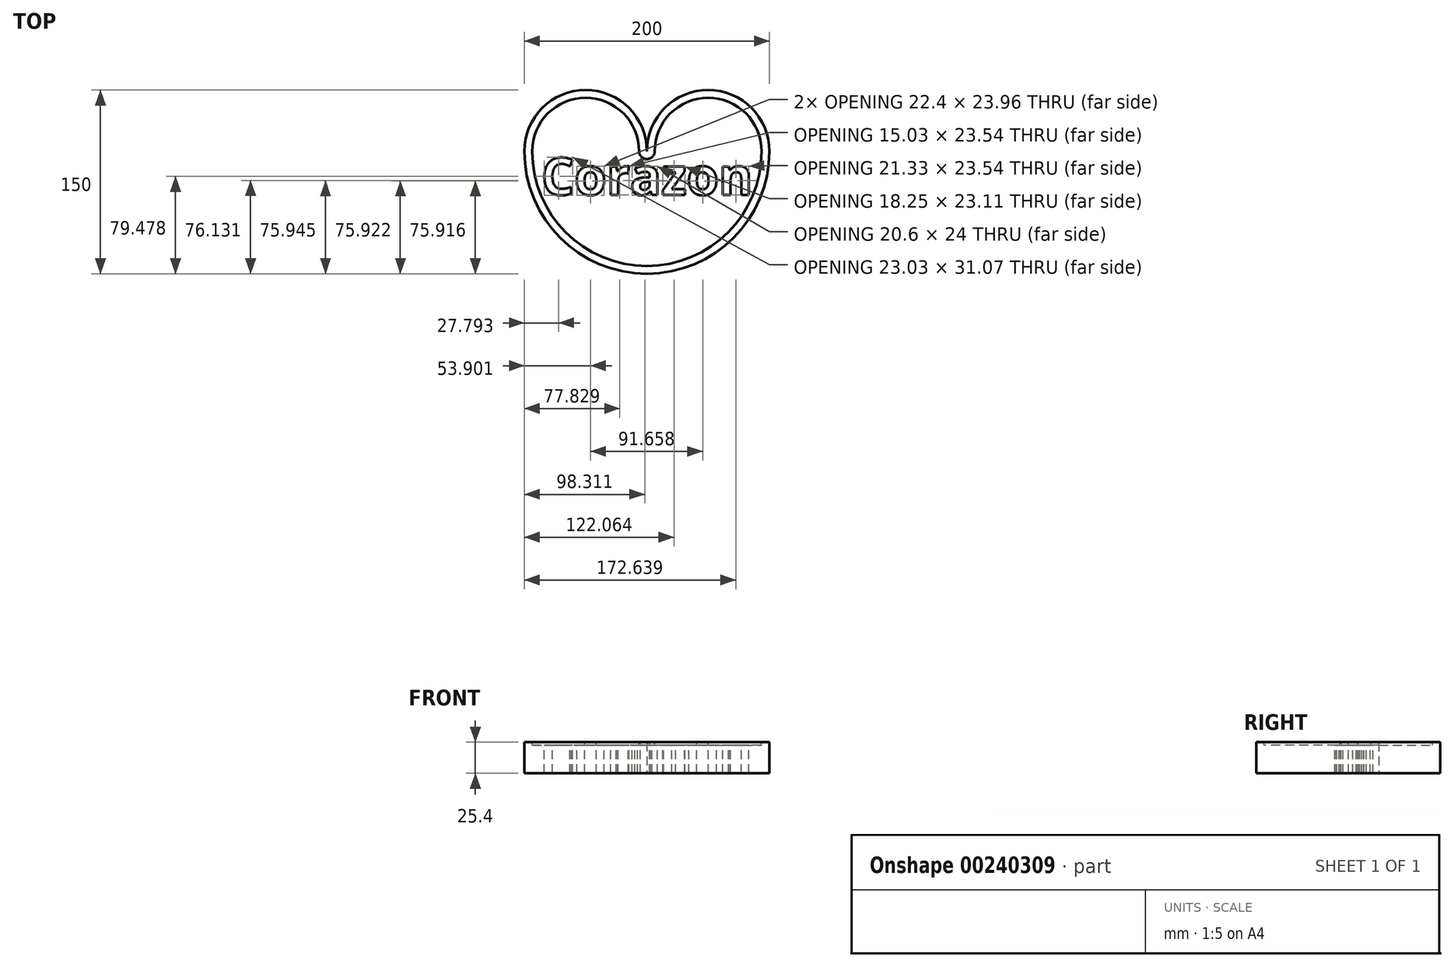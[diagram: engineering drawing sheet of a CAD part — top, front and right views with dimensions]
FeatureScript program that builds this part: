
annotation { "Feature Type Name" : "Feature", "Feature Type Description" : "" }
export const myFeature = defineFeature(function(context is Context, id is Id, definition is map)
    precondition{}
    {
        {
            var Q0;
            Q0=qCreatedBy(makeId("Top.planeOp"),FACE);
            var sketch = newSketch(context, id + "F0", { "sketchPlane" : qUnion([Q0])});
            skLineSegment(sketch, "E0.bottom", {"start": v(50, 50) * mm, "end": v(-50, 50) * mm, "construction": true});
            skLineSegment(sketch, "E0.top", {"start": v(50, -50) * mm, "end": v(-50, -50) * mm, "construction": true});
            skLineSegment(sketch, "E0.left", {"start": v(50, 50) * mm, "end": v(50, -50) * mm, "construction": true});
            skLineSegment(sketch, "E0.right", {"start": v(-50, 50) * mm, "end": v(-50, -50) * mm, "construction": true});
            skPoint(sketch, "E0.middle", {"position": v(0, 0) * mm});
            skArc(sketch, "E1", {"start": v(0, 50) * mm, "mid": v(-50, 100) * mm, "end": v(-100, 50) * mm});
            skArc(sketch, "E2", {"start": v(100, 50) * mm, "mid": v(50, 100) * mm, "end": v(0, 50) * mm});
            skLineSegment(sketch, "E3", {"start": v(-50, 50) * mm, "end": v(50, 50) * mm, "construction": true});
            skPoint(sketch, "E4.start.orphan", {"position": v(50, 0) * mm});
            skPoint(sketch, "E5.start.orphan", {"position": v(-50, 0) * mm});
            skArc(sketch, "E6", {"start": v(-100, 50) * mm, "mid": v(0, -50) * mm, "end": v(100, 50) * mm});
            skSolve(sketch);
        }
        {
            var Q0;
            Q0 = qSketchRegion(id + "F0", true);
            extrude(context, id + "F1", {"entities" : qUnion([Q0]), "depth" : 25.4 * mm});
        }
        {
            var Q0;
            Q0=makeQuery(id+"F1.opExtrude","CAP_FACE",FACE,{"disambiguationData":[OSD([sQuery(id+"F0.wireOp",EDGE,"E1"),sQuery(id+"F0.wireOp",EDGE,"E2"),sQuery(id+"F0.wireOp",EDGE,"E6")])],"isStart":false});
            var sketch = newSketch(context, id + "F2", { "sketchPlane" : qUnion([Q0])});
            skText(sketch, "E7", { "text": "Corazon", "fontName": "OpenSans-Bold.ttf"});
            const initialGuessF2  = {"E7": [-0.08618, 0.01436, 1, 0, 0.03048]};
            skSetInitialGuess(sketch, initialGuessF2);
            skSolve(sketch);
        }
        {
            var Q0;
            Q0 = qSketchRegion(id + "F2", true);
            extrude(context, id + "F3", {"entities" : qUnion([Q0]), "operationType" : NewBodyOperationType.REMOVE, "oppositeDirection" : true, "depth" : 25.4 * mm});
        }
        {
            var Q0;
            {var subQ0=sQuery(id+"F0.wireOp",EDGE,"E1");var subQ1=sQuery(id+"F0.wireOp",EDGE,"E2");var subQ2=sQuery(id+"F0.wireOp",EDGE,"E6");Q0=makeQuery(id+"F3.boolean.opBoolean","SPLIT",FACE,{"disambiguationData":[TD([makeQuery(id+"F1.opExtrude","SWEPT_FACE",FACE,{"disambiguationData":[OSD([subQ0])]})])],"derivedFrom":makeQuery(id+"F1.opExtrude","CAP_FACE",FACE,{"disambiguationData":[OSD([subQ0,subQ1,subQ2])],"isStart":false})});}
            var sketch = newSketch(context, id + "F4", { "sketchPlane" : qUnion([Q0])});
            skArc(sketch, "E8.JHh.JHh", {"start": v(-100, 50) * mm, "mid": v(0, -50) * mm, "end": v(100, 50) * mm, "construction": true});
            skArc(sketch, "E8.JHZ.JHZ", {"start": v(100, 50) * mm, "mid": v(50, 100) * mm, "end": v(0, 50) * mm, "construction": true});
            skArc(sketch, "E8.JHR.JHR", {"start": v(0, 50) * mm, "mid": v(-50, 100) * mm, "end": v(-100, 50) * mm, "construction": true});
            skArc(sketch, "E8.0.startCap", {"start": v(-106.35, 50) * mm, "mid": v(-100, 56.35) * mm, "end": v(-93.65, 50) * mm});
            skArc(sketch, "E8.0.endCap", {"start": v(93.65, 50) * mm, "mid": v(100, 56.35) * mm, "end": v(106.35, 50) * mm});
            skArc(sketch, "E8.0.left", {"start": v(-93.65, 50) * mm, "mid": v(0, -43.65) * mm, "end": v(93.65, 50) * mm});
            skArc(sketch, "E8.0.right", {"start": v(-106.35, 50) * mm, "mid": v(0, -56.35) * mm, "end": v(106.35, 50) * mm});
            skArc(sketch, "E8.1.startCap", {"start": v(106.35, 50) * mm, "mid": v(100, 43.65) * mm, "end": v(93.65, 50) * mm});
            skArc(sketch, "E8.1.endCap", {"start": v(6.35, 50) * mm, "mid": v(0, 43.65) * mm, "end": v(-6.35, 50) * mm});
            skArc(sketch, "E8.1.left", {"start": v(93.65, 50) * mm, "mid": v(50, 93.65) * mm, "end": v(6.35, 50) * mm});
            skArc(sketch, "E8.1.right", {"start": v(106.35, 50) * mm, "mid": v(50, 106.35) * mm, "end": v(-6.35, 50) * mm});
            skArc(sketch, "E8.2.startCap", {"start": v(6.35, 50) * mm, "mid": v(0, 43.65) * mm, "end": v(-6.35, 50) * mm});
            skArc(sketch, "E8.2.endCap", {"start": v(-93.65, 50) * mm, "mid": v(-100, 43.65) * mm, "end": v(-106.35, 50) * mm});
            skArc(sketch, "E8.2.left", {"start": v(-6.35, 50) * mm, "mid": v(-50, 93.65) * mm, "end": v(-93.65, 50) * mm});
            skArc(sketch, "E8.2.right", {"start": v(6.35, 50) * mm, "mid": v(-50, 106.35) * mm, "end": v(-106.35, 50) * mm});
            skSolve(sketch);
        }
        {
            var Q0;
            Q0=makeQuery(id+"F4.imprint","IMPRINT",FACE,{"disambiguationData":[TD([[makeQuery(id+"F4.imprint","IMPRINT",EDGE,{"derivedFrom":sQuery(id+"F4.wireOp",EDGE,"E8.0.left")}),1.0]])]});
            extrude(context, id + "F5", {"entities" : qUnion([Q0]), "operationType" : NewBodyOperationType.REMOVE, "oppositeDirection" : true, "depth" : 2.54 * mm});
        }
    });
